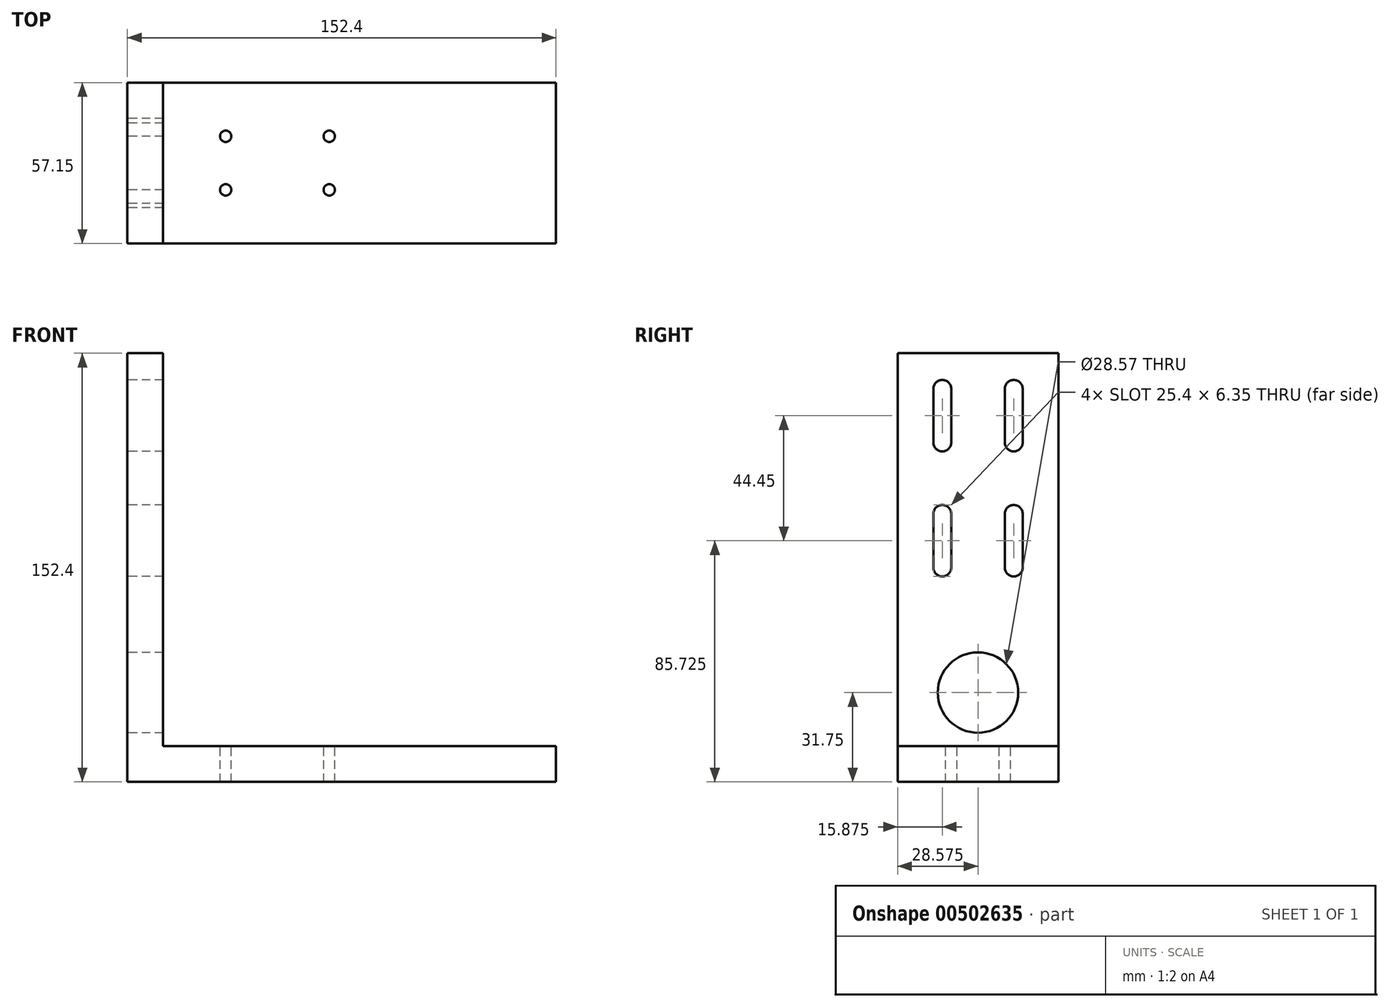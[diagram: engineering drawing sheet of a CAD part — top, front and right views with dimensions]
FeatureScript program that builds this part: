
annotation { "Feature Type Name" : "Feature", "Feature Type Description" : "" }
export const myFeature = defineFeature(function(context is Context, id is Id, definition is map)
    precondition{}
    {
        {
            var Q0;
            Q0=qCreatedBy(makeId("Right.planeOp"),FACE);
            var sketch = newSketch(context, id + "F0", { "sketchPlane" : qUnion([Q0])});
            skLineSegment(sketch, "E0.bottom", {"start": v(0, 0) * mm, "end": v(57.15, 0) * mm});
            skLineSegment(sketch, "E0.top", {"start": v(0, 139.7) * mm, "end": v(57.15, 139.7) * mm});
            skLineSegment(sketch, "E0.left", {"start": v(0, 0) * mm, "end": v(0, 139.7) * mm});
            skLineSegment(sketch, "E0.right", {"start": v(57.15, 0) * mm, "end": v(57.15, 139.7) * mm});
            skCircle(sketch, "E1", {"center": v(28.58, 19.05) * mm, "radius": 14.29 * mm});
            skLineSegment(sketch, "E2", {"start": v(12.7, 63.5) * mm, "end": v(12.7, 82.55) * mm});
            skLineSegment(sketch, "E3", {"start": v(19.05, 82.55) * mm, "end": v(19.05, 63.5) * mm});
            skArc(sketch, "E4", {"start": v(19.05, 82.55) * mm, "mid": v(15.88, 85.73) * mm, "end": v(12.7, 82.55) * mm});
            skArc(sketch, "E5", {"start": v(12.7, 63.5) * mm, "mid": v(15.88, 60.33) * mm, "end": v(19.05, 63.5) * mm});
            skLineSegment(sketch, "E6", {"start": v(38.1, 63.5) * mm, "end": v(38.1, 82.55) * mm});
            skLineSegment(sketch, "E7", {"start": v(44.45, 82.55) * mm, "end": v(44.45, 63.5) * mm});
            skArc(sketch, "E8", {"start": v(44.45, 82.55) * mm, "mid": v(41.27, 85.73) * mm, "end": v(38.1, 82.55) * mm});
            skArc(sketch, "E9", {"start": v(38.1, 63.5) * mm, "mid": v(41.27, 60.33) * mm, "end": v(44.45, 63.5) * mm});
            skLineSegment(sketch, "E10", {"start": v(38.1, 107.95) * mm, "end": v(38.1, 127) * mm});
            skLineSegment(sketch, "E11", {"start": v(44.45, 127) * mm, "end": v(44.45, 107.95) * mm});
            skArc(sketch, "E12", {"start": v(44.45, 127) * mm, "mid": v(41.27, 130.18) * mm, "end": v(38.1, 127) * mm});
            skArc(sketch, "E13", {"start": v(38.1, 107.95) * mm, "mid": v(41.27, 104.78) * mm, "end": v(44.45, 107.95) * mm});
            skLineSegment(sketch, "E14", {"start": v(12.7, 107.95) * mm, "end": v(12.7, 127) * mm});
            skLineSegment(sketch, "E15", {"start": v(19.05, 127) * mm, "end": v(19.05, 107.95) * mm});
            skArc(sketch, "E16", {"start": v(19.05, 127) * mm, "mid": v(15.88, 130.18) * mm, "end": v(12.7, 127) * mm});
            skArc(sketch, "E17", {"start": v(12.7, 107.95) * mm, "mid": v(15.88, 104.78) * mm, "end": v(19.05, 107.95) * mm});
            skSolve(sketch);
        }
        {
            var Q0;
            Q0=makeQuery(id+"F0.imprint","IMPRINT",FACE,{"disambiguationData":[TD([[makeQuery(id+"F0.imprint","IMPRINT",EDGE,{"derivedFrom":sQuery(id+"F0.wireOp",EDGE,"E0.bottom")}),1.0]])]});
            extrude(context, id + "F1", {"entities" : qUnion([Q0]), "depth" : 12.7 * mm});
        }
        {
            var Q0;
            Q0=makeQuery(id+"F1.opExtrude","SWEPT_FACE",FACE,{"disambiguationData":[OSD([sQuery(id+"F0.wireOp",EDGE,"E0.bottom")])]});
            var sketch = newSketch(context, id + "F2", { "sketchPlane" : qUnion([Q0])});
            skLineSegment(sketch, "E18.bottom", {"start": v(0, 0) * mm, "end": v(152.4, 0) * mm});
            skLineSegment(sketch, "E18.top", {"start": v(0, -57.15) * mm, "end": v(152.4, -57.15) * mm});
            skLineSegment(sketch, "E18.left", {"start": v(0, 0) * mm, "end": v(0, -57.15) * mm});
            skLineSegment(sketch, "E18.right", {"start": v(152.4, 0) * mm, "end": v(152.4, -57.15) * mm});
            skCircle(sketch, "E19", {"center": v(34.93, -19.05) * mm, "radius": 2.02 * mm});
            skCircle(sketch, "E20", {"center": v(71.76, -19.05) * mm, "radius": 2.02 * mm});
            skCircle(sketch, "E21", {"center": v(71.76, -38.1) * mm, "radius": 2.02 * mm});
            skCircle(sketch, "E22", {"center": v(34.93, -38.1) * mm, "radius": 2.02 * mm});
            skPoint(sketch, "E23", {"position": v(34.93, -28.58) * mm});
            skSolve(sketch);
        }
        {
            var Q0;
            {var subQ2=sQuery(id+"F2.wireOp",EDGE,"E18.right");Q0=makeQuery(id+"F2.imprint","IMPRINT",FACE,{"disambiguationData":[TD([[makeQuery(id+"F2.imprint","IMPRINT",EDGE,{"derivedFrom":subQ2}),-1.0]])]});}
            var Q1;
            {var subQ0=sQuery(id+"F2.wireOp",EDGE,"E18.left");Q1=makeQuery(id+"F2.imprint","IMPRINT",FACE,{"disambiguationData":[TD([[makeQuery(id+"F2.imprint","IMPRINT",EDGE,{"derivedFrom":subQ0}),1.0]])]});}
            extrude(context, id + "F3", {"entities" : qUnion([Q0, Q1]), "operationType" : NewBodyOperationType.ADD, "depth" : 12.7 * mm});
        }
    });
